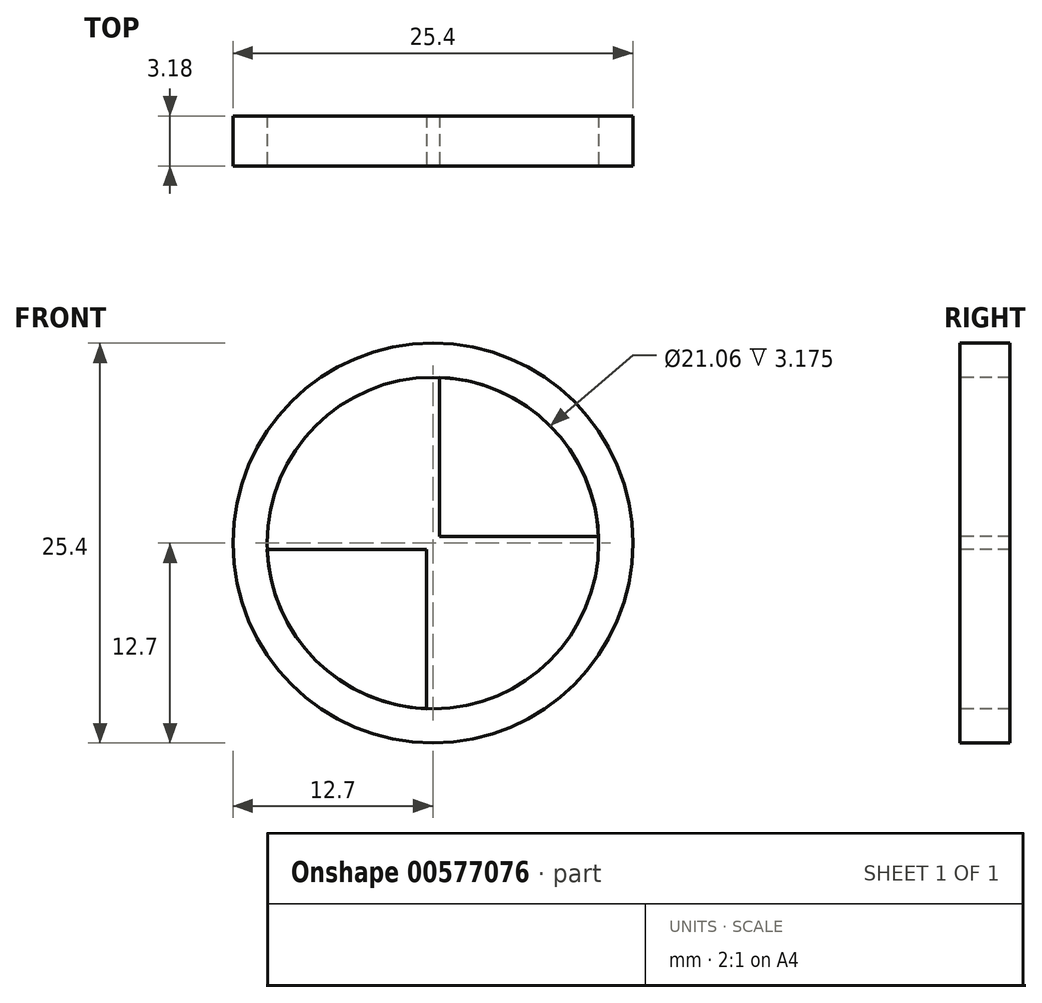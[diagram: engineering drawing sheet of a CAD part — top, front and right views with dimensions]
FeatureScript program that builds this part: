
annotation { "Feature Type Name" : "Feature", "Feature Type Description" : "" }
export const myFeature = defineFeature(function(context is Context, id is Id, definition is map)
    precondition{}
    {
        {
            var Q0;
            Q0=qCreatedBy(makeId("Front.planeOp"),FACE);
            var sketch = newSketch(context, id + "F0", { "sketchPlane" : qUnion([Q0])});
            skCircle(sketch, "E0", {"center": v(0, 0) * mm, "radius": 12.7 * mm});
            skSolve(sketch);
        }
        {
            var Q0;
            Q0 = qSketchRegion(id + "F0", true);
            extrude(context, id + "F1", {"entities" : qUnion([Q0]), "depth" : 3.17 * mm, "offsetDistance" : 25.4 * mm});
        }
        {
            var Q0;
            Q0=makeQuery(id+"F1.opExtrude","CAP_FACE",FACE,{"disambiguationData":[OSD([sQuery(id+"F0.wireOp",EDGE,"E0")])],"isStart":false});
            var sketch = newSketch(context, id + "F2", { "sketchPlane" : qUnion([Q0])});
            skCircle(sketch, "E1", {"center": v(0, 0) * mm, "radius": 10.53 * mm});
            skSolve(sketch);
        }
        {
            var Q0;
            Q0 = qSketchRegion(id + "F2", true);
            extrude(context, id + "F3", {"entities" : qUnion([Q0]), "operationType" : NewBodyOperationType.REMOVE, "oppositeDirection" : true, "depth" : 25.4 * mm, "offsetDistance" : 25.4 * mm});
        }
        {
            var Q0;
            Q0=makeQuery(id+"F1.opExtrude","CAP_FACE",FACE,{"disambiguationData":[OSD([sQuery(id+"F0.wireOp",EDGE,"E0")])],"isStart":false});
            var sketch = newSketch(context, id + "F4", { "sketchPlane" : qUnion([Q0])});
            skLineSegment(sketch, "E2.bottom", {"start": v(0.4, -10.52) * mm, "end": v(-0.4, -10.52) * mm});
            skLineSegment(sketch, "E2.top", {"start": v(0.4, 10.52) * mm, "end": v(-0.4, 10.52) * mm});
            skLineSegment(sketch, "E2.left", {"start": v(0.4, -10.52) * mm, "end": v(0.4, 10.52) * mm});
            skLineSegment(sketch, "E2.right", {"start": v(-0.4, -10.52) * mm, "end": v(-0.4, 10.52) * mm});
            skPoint(sketch, "E2.middle", {"position": v(0, 0) * mm});
            skLineSegment(sketch, "E3.bottom", {"start": v(10.52, -0.4) * mm, "end": v(-10.52, -0.4) * mm});
            skLineSegment(sketch, "E3.top", {"start": v(10.52, 0.4) * mm, "end": v(-10.52, 0.4) * mm});
            skLineSegment(sketch, "E3.left", {"start": v(10.52, -0.4) * mm, "end": v(10.52, 0.4) * mm});
            skLineSegment(sketch, "E3.right", {"start": v(-10.52, -0.4) * mm, "end": v(-10.52, 0.4) * mm});
            skSolve(sketch);
        }
        {
            var Q0;
            {var subQ0=sQuery(id+"F4.wireOp",EDGE,"E2.left");var subQ3=sQuery(id+"F4.wireOp",EDGE,"E3.top");var subQ4=makeQuery(id+"F4.imprint","INTERSECT",VERTEX,{"derivedFrom":[subQ0,subQ3]});Q0=makeQuery(id+"F4.imprint","IMPRINT",FACE,{"disambiguationData":[TD([[makeQuery(id+"F4.imprint","IMPRINT",EDGE,{"disambiguationData":[TD([[subQ4,-1.0]])],"derivedFrom":subQ0}),-1.0]])]});}
            var Q1;
            {var subQ0=sQuery(id+"F4.wireOp",EDGE,"E2.right");var subQ3=sQuery(id+"F4.wireOp",EDGE,"E3.bottom");var subQ4=makeQuery(id+"F4.imprint","INTERSECT",VERTEX,{"derivedFrom":[subQ0,subQ3]});Q1=makeQuery(id+"F4.imprint","IMPRINT",FACE,{"disambiguationData":[TD([[makeQuery(id+"F4.imprint","IMPRINT",EDGE,{"disambiguationData":[TD([[subQ4,1.0]])],"derivedFrom":subQ0}),1.0]])]});}
            extrude(context, id + "F5", {"entities" : qUnion([Q0, Q1]), "oppositeDirection" : true, "depth" : 3.17 * mm, "offsetDistance" : 25.4 * mm});
        }
    });
